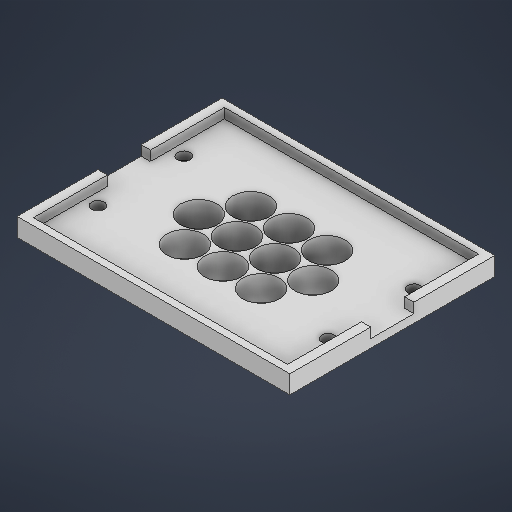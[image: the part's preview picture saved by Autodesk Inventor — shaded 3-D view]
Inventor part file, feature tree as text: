
AUTODESK INVENTOR PART (.ipt)
format: ipt  version: 2025.2 (Build 292293000, 293)  size: 666,624 bytes
history: native  units: mm
features: extrude x6, sketch x6, projected_geometry x3
ambient origin geometry x8: Origin, YZ Plane, XZ Plane, XY Plane, X Axis, Y Axis, Z Axis, Center Point
bodies: Solid1 (feature_tree)
feature tree (15):
  extrude  "Extrusion1"  Depth=1.0mm
  extrude  "Extrusion2"  Depth=1.0mm
  extrude  "Extrusion3"  Depth=1.0mm
  extrude  "Extrusion4"  Depth=24.0mm
  extrude  "Extrusion5"  Depth=24.0mm
  extrude  "Extrusion6"  Depth=6.0mm
  sketch  "Sketch1"  dims[d0=22.0mm d1=1.0mm]
  sketch  "Sketch2"  dims[d2=22.0mm d3=1.0mm]
  sketch  "Sketch3"  dims[d4=22.0mm d5=1.0mm]
  projected_geometry  "Projected Loop1"
  sketch  "Sketch4"  dims[d6=22.0mm d7=24.0mm]
  projected_geometry  "Projected Loop2"
  sketch  "Sketch5"  dims[d8=24.0mm d9=24.0mm]
  sketch  "Sketch6"  dims[d10=24.0mm d11=22.0mm d12=22.0mm d16=22.0mm d17=22.0mm d19=24.0mm d21=24.0mm d22=24.0mm d23=24.0mm d25=26.0mm d27=26.0mm d28=26.0mm d29=26.0mm d30=26.0mm d31=26.0mm d32=26.0mm d33=26.0mm d34=15.0mm d35=0.0mm d36=115.3mm d37=153.4mm d38=5.0mm d39=0.0mm d44=6.0mm d45=5.0mm d46=0.0mm d47=0.0mm d56=7.73mm d57=7.73mm d58=7.73mm d59=7.73mm d60=0.0mm d61=0.0mm d62=7.228mm d63=31.75mm d64=7.228mm d65=7.228mm d66=31.75mm d67=24.0mm d71=24.0mm d72=22.0mm d73=22.0mm d74=0.0mm d75=0.0mm d76=30.0mm d77=20.0mm d78=20.0mm d79=20.0mm d80=15.0mm d81=15.0mm d82=30.0mm d83=20.0mm d84=14.0mm d85=14.0mm d86=6.0mm d87=0.0mm]
  projected_geometry  "Projected Loop3"
